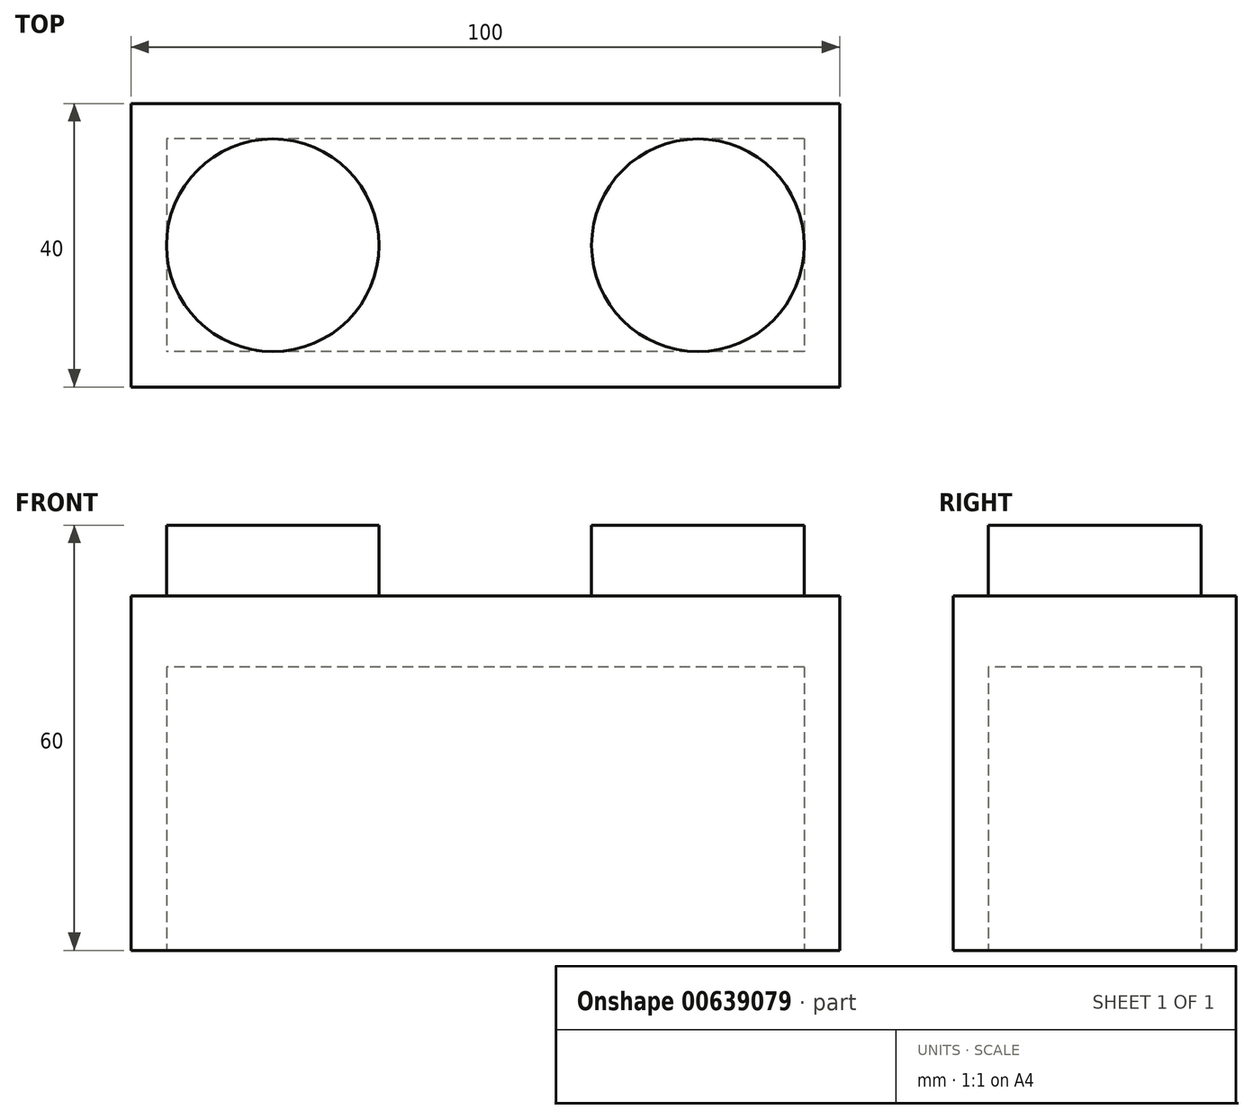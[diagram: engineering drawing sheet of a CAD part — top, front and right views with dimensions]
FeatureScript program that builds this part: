
annotation { "Feature Type Name" : "Feature", "Feature Type Description" : "" }
export const myFeature = defineFeature(function(context is Context, id is Id, definition is map)
    precondition{}
    {
        {
            var Q0;
            Q0=qCreatedBy(makeId("Top.planeOp"),FACE);
            var sketch = newSketch(context, id + "F0", { "sketchPlane" : qUnion([Q0])});
            skLineSegment(sketch, "E0.bottom", {"start": v(50, -20) * mm, "end": v(-50, -20) * mm});
            skLineSegment(sketch, "E0.top", {"start": v(50, 20) * mm, "end": v(-50, 20) * mm});
            skLineSegment(sketch, "E0.left", {"start": v(50, -20) * mm, "end": v(50, 20) * mm});
            skLineSegment(sketch, "E0.right", {"start": v(-50, -20) * mm, "end": v(-50, 20) * mm});
            skPoint(sketch, "E0.middle", {"position": v(0, 0) * mm});
            skSolve(sketch);
        }
        {
            var Q0;
            Q0 = qSketchRegion(id + "F0", true);
            extrude(context, id + "F1", {"entities" : qUnion([Q0]), "depth" : 50 * mm, "offsetDistance" : 25 * mm});
        }
        {
            var Q0;
            Q0=makeQuery(id+"F1.opExtrude","CAP_FACE",FACE,{"disambiguationData":[OSD([sQuery(id+"F0.wireOp",EDGE,"E0.bottom"),sQuery(id+"F0.wireOp",EDGE,"E0.top"),sQuery(id+"F0.wireOp",EDGE,"E0.left"),sQuery(id+"F0.wireOp",EDGE,"E0.right")])],"isStart":false});
            var sketch = newSketch(context, id + "F2", { "sketchPlane" : qUnion([Q0])});
            skCircle(sketch, "E1", {"center": v(-30, 0) * mm, "radius": 15 * mm});
            skCircle(sketch, "E2", {"center": v(30, 0) * mm, "radius": 15 * mm});
            skSolve(sketch);
        }
        {
            var Q0;
            Q0=makeQuery(id+"F2.imprint","IMPRINT",FACE,{"disambiguationData":[TD([[makeQuery(id+"F2.imprint","IMPRINT",EDGE,{"derivedFrom":sQuery(id+"F2.wireOp",EDGE,"E2")}),1.0]])]});
            var Q1;
            Q1=makeQuery(id+"F2.imprint","IMPRINT",FACE,{"disambiguationData":[TD([[makeQuery(id+"F2.imprint","IMPRINT",EDGE,{"derivedFrom":sQuery(id+"F2.wireOp",EDGE,"E1")}),1.0]])]});
            extrude(context, id + "F3", {"entities" : qUnion([Q0, Q1]), "operationType" : NewBodyOperationType.ADD, "depth" : 10 * mm, "offsetDistance" : 25 * mm});
        }
        {
            var Q0;
            Q0=makeQuery(id+"F1.opExtrude","CAP_FACE",FACE,{"disambiguationData":[OSD([sQuery(id+"F0.wireOp",EDGE,"E0.bottom"),sQuery(id+"F0.wireOp",EDGE,"E0.top"),sQuery(id+"F0.wireOp",EDGE,"E0.left"),sQuery(id+"F0.wireOp",EDGE,"E0.right")])],"isStart":true});
            var sketch = newSketch(context, id + "F4", { "sketchPlane" : qUnion([Q0])});
            skLineSegment(sketch, "E3.bottom", {"start": v(45, -15) * mm, "end": v(-45, -15) * mm});
            skLineSegment(sketch, "E3.top", {"start": v(45, 15) * mm, "end": v(-45, 15) * mm});
            skLineSegment(sketch, "E3.left", {"start": v(45, -15) * mm, "end": v(45, 15) * mm});
            skLineSegment(sketch, "E3.right", {"start": v(-45, -15) * mm, "end": v(-45, 15) * mm});
            skPoint(sketch, "E3.middle", {"position": v(0, 0) * mm});
            skSolve(sketch);
        }
        {
            var Q0;
            Q0=makeQuery(id+"F4.imprint","IMPRINT",FACE,{"disambiguationData":[TD([[makeQuery(id+"F4.imprint","IMPRINT",EDGE,{"derivedFrom":sQuery(id+"F4.wireOp",EDGE,"E3.bottom")}),-1.0]])]});
            extrude(context, id + "F5", {"entities" : qUnion([Q0]), "operationType" : NewBodyOperationType.REMOVE, "oppositeDirection" : true, "depth" : 40 * mm, "offsetDistance" : 25 * mm});
        }
    });
